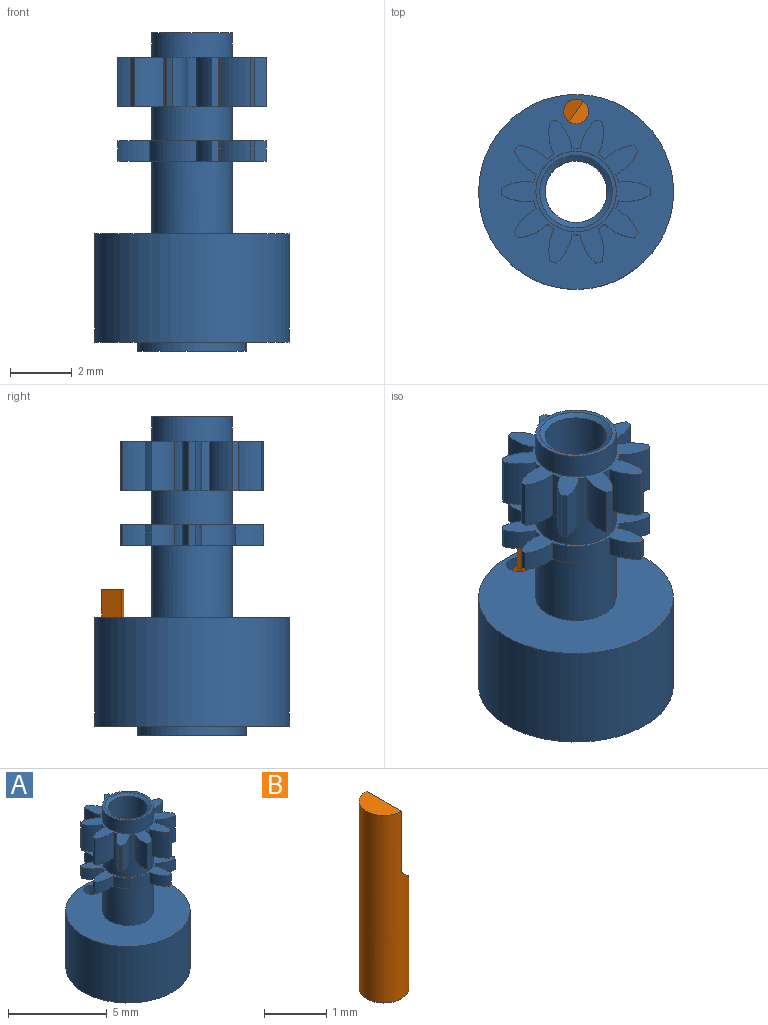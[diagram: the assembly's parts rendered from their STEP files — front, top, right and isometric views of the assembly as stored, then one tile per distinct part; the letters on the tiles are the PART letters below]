
ASSEMBLY  parts=2 mates=1
PART A: 89 faces, bbox 6.3x6.3x10.3 mm
  f0: cylinder r=1.3mm len=2.6mm, axis (0,0,-1), area 6.5mm2, adj f10,f47
  f1: cylinder r=1.3mm len=2.6mm, axis (0,0,-1), area 9mm2, adj f13,f88
  f2: cylinder r=1mm len=9.51mm, axis (0,0,-1), area 59.7mm2, adj f3,f12
  f3: cone r=1mm half-angle=30deg, axis (0,0,-1), area 6mm2, adj f2,f4
  f4: plane 3.5x3.5mm, normal (0,0,-1), area 3.5mm2, adj f3,f5
  f5: cylinder r=1.75mm len=3.5mm, axis (0,0,-1), area 3.3mm2, adj f4,f6
  f6: plane 6.3x6.3mm, normal (0,0,-1), area 21mm2, adj f5,f7,f11
  f7: cylinder r=3.15mm len=6.3mm, axis (0,0,-1), area 69.3mm2, adj f6,f8
  f8: plane 6.3x6.3mm, normal (0,0,1), area 25.4mm2, adj f7,f9,f11
  f9: cylinder r=1.3mm len=2.6mm, axis (0,0,-1), area 19.2mm2, adj f8,f46
  f10: plane 2.6x2.6mm, normal (0,0,1), area 1mm2, adj f0,f12
  f11: cylinder r=0.4mm len=3.5mm, axis (0,0,1), area 8.8mm2, adj f6,f8
  f12: cone r=1.17mm half-angle=60deg, axis (0,0,1), area 1.4mm2, adj f2,f10
  f13: plane 4.8x4.63mm, normal (0,0,1), area 5.2mm2, adj f1,f14,f15,f16,f17,f18,f19,f20
  f14: cylinder r=1.5mm len=1.03mm, axis (0,0,-1), area 0.7mm2, adj f13,f15,f45,f46
  f15: cylinder r=1.4mm len=1.5mm, axis (0,0,-1), area 1.3mm2, adj f13,f14,f16,f46
  f16: cylinder r=1.5mm len=0.92mm, axis (0,0,-1), area 0.7mm2, adj f13,f15,f17,f46
  f17: cylinder r=2.4mm len=0.65mm, axis (0,0,-1), area 0.1mm2, adj f13,f16,f18,f46
  f18: cylinder r=1.5mm len=1.04mm, axis (0,0,-1), area 0.7mm2, adj f13,f17,f19,f46
  f19: cylinder r=1.4mm len=0.65mm, axis (0,0,-1), area 0.2mm2, adj f13,f18,f20,f46
  f20: cylinder r=1.5mm len=0.95mm, axis (0,0,-1), area 0.7mm2, adj f13,f19,f21,f46
  f21: cylinder r=2.4mm len=0.65mm, axis (0,0,-1), area 0.1mm2, adj f13,f20,f22,f46
  f22: cylinder r=1.5mm len=0.77mm, axis (0,0,-1), area 0.7mm2, adj f13,f21,f23,f46
  f23: cylinder r=1.4mm len=0.65mm, axis (0,0,-1), area 0.2mm2, adj f13,f22,f24,f46
  f24: cylinder r=1.5mm len=1.03mm, axis (0,0,-1), area 0.7mm2, adj f13,f23,f25,f46
  f25: cylinder r=2.4mm len=0.65mm, axis (0,0,-1), area 0.1mm2, adj f13,f24,f26,f46
  f26: cylinder r=1.5mm len=1.03mm, axis (0,0,-1), area 0.7mm2, adj f13,f25,f27,f46
  f27: cylinder r=1.4mm len=0.65mm, axis (0,0,-1), area 0.2mm2, adj f13,f26,f28,f46
  f28: cylinder r=1.5mm len=0.77mm, axis (0,0,-1), area 0.7mm2, adj f13,f27,f29,f46
  f29: cylinder r=2.4mm len=0.65mm, axis (0,0,-1), area 0.1mm2, adj f13,f28,f30,f46
  f30: cylinder r=1.5mm len=0.95mm, axis (0,0,-1), area 0.7mm2, adj f13,f29,f31,f46
  f31: cylinder r=1.4mm len=0.65mm, axis (0,0,-1), area 0.2mm2, adj f13,f30,f32,f46
  f32: cylinder r=1.5mm len=1.04mm, axis (0,0,-1), area 0.7mm2, adj f13,f31,f33,f46
  f33: cylinder r=2.4mm len=0.65mm, axis (0,0,-1), area 0.1mm2, adj f13,f32,f34,f46
  f34: cylinder r=1.5mm len=0.92mm, axis (0,0,-1), area 0.7mm2, adj f13,f33,f35,f46
  f35: cylinder r=1.4mm len=0.65mm, axis (0,0,-1), area 0.2mm2, adj f13,f34,f36,f46
  f36: cylinder r=1.5mm len=0.92mm, axis (0,0,-1), area 0.7mm2, adj f13,f35,f37,f46
  f37: cylinder r=2.4mm len=0.65mm, axis (0,0,-1), area 0.1mm2, adj f13,f36,f38,f46
  f38: cylinder r=1.5mm len=1.04mm, axis (0,0,-1), area 0.7mm2, adj f13,f37,f39,f46
  f39: cylinder r=1.4mm len=0.65mm, axis (0,0,-1), area 0.2mm2, adj f13,f38,f40,f46
  f40: cylinder r=1.5mm len=0.95mm, axis (0,0,-1), area 0.7mm2, adj f13,f39,f41,f46
  f41: cylinder r=2.4mm len=0.65mm, axis (0,0,-1), area 0.1mm2, adj f13,f40,f42,f46
  f42: cylinder r=1.5mm len=0.77mm, axis (0,0,-1), area 0.7mm2, adj f13,f41,f43,f46
  f43: cylinder r=1.4mm len=0.65mm, axis (0,0,-1), area 0.2mm2, adj f13,f42,f44,f46
  f44: cylinder r=1.5mm len=1.03mm, axis (0,0,-1), area 0.7mm2, adj f13,f43,f45,f46
  f45: cylinder r=2.4mm len=0.65mm, axis (0,0,-1), area 0.1mm2, adj f13,f14,f44,f46
  f46: plane 4.8x4.63mm, normal (0,0,-1), area 5.2mm2, adj f9,f14,f15,f16,f17,f18,f19,f20
  f47: plane 4.8x4.63mm, normal (0,0,1), area 6.3mm2, adj f0,f48,f49,f50,f51,f52,f53,f54
  f48: cylinder r=1.5mm len=1.6mm, axis (0,0,-1), area 1.7mm2, adj f47,f49,f87,f88
  f49: cylinder r=1.4mm len=1.6mm, axis (0,0,-1), area 0.4mm2, adj f47,f48,f50,f88
  f50: cylinder r=1.5mm len=1.6mm, axis (0,0,-1), area 1.7mm2, adj f47,f49,f54,f88
  f51: cylinder r=1.5mm len=1.6mm, axis (0,0,-1), area 1.7mm2, adj f47,f52,f54,f88
  f52: cylinder r=1.4mm len=1.6mm, axis (0,0,-1), area 0.4mm2, adj f47,f51,f53,f88
  f53: cylinder r=1.5mm len=1.6mm, axis (0,0,-1), area 1.7mm2, adj f47,f52,f58,f88
  f54: cylinder r=2.4mm len=1.6mm, axis (0,0,-1), area 0.3mm2, adj f47,f50,f51,f88
  f55: cylinder r=1.5mm len=1.6mm, axis (0,0,-1), area 1.7mm2, adj f47,f56,f58,f88
  f56: cylinder r=1.4mm len=1.6mm, axis (0,0,-1), area 0.4mm2, adj f47,f55,f57,f88
  f57: cylinder r=1.5mm len=1.6mm, axis (0,0,-1), area 1.7mm2, adj f47,f56,f62,f88
  f58: cylinder r=2.4mm len=1.6mm, axis (0,0,-1), area 0.3mm2, adj f47,f53,f55,f88
  f59: cylinder r=1.5mm len=1.6mm, axis (0,0,-1), area 1.7mm2, adj f47,f60,f62,f88
  f60: cylinder r=1.4mm len=1.6mm, axis (0,0,-1), area 0.4mm2, adj f47,f59,f61,f88
  f61: cylinder r=1.5mm len=1.6mm, axis (0,0,-1), area 1.7mm2, adj f47,f60,f66,f88
  f62: cylinder r=2.4mm len=1.6mm, axis (0,0,-1), area 0.3mm2, adj f47,f57,f59,f88
  f63: cylinder r=1.5mm len=1.6mm, axis (0,0,-1), area 1.7mm2, adj f47,f64,f66,f88
  f64: cylinder r=1.4mm len=1.6mm, axis (0,0,-1), area 0.4mm2, adj f47,f63,f65,f88
  f65: cylinder r=1.5mm len=1.6mm, axis (0,0,-1), area 1.7mm2, adj f47,f64,f70,f88
  f66: cylinder r=2.4mm len=1.6mm, axis (0,0,-1), area 0.3mm2, adj f47,f61,f63,f88
  f67: cylinder r=1.5mm len=1.6mm, axis (0,0,-1), area 1.7mm2, adj f47,f68,f70,f88
  f68: cylinder r=1.4mm len=1.6mm, axis (0,0,-1), area 0.4mm2, adj f47,f67,f69,f88
  f69: cylinder r=1.5mm len=1.6mm, axis (0,0,-1), area 1.7mm2, adj f47,f68,f74,f88
  f70: cylinder r=2.4mm len=1.6mm, axis (0,0,-1), area 0.3mm2, adj f47,f65,f67,f88
  f71: cylinder r=1.5mm len=1.6mm, axis (0,0,-1), area 1.7mm2, adj f47,f72,f74,f88
  f72: cylinder r=1.4mm len=1.6mm, axis (0,0,-1), area 0.4mm2, adj f47,f71,f73,f88
  f73: cylinder r=1.5mm len=1.6mm, axis (0,0,-1), area 1.7mm2, adj f47,f72,f78,f88
  f74: cylinder r=2.4mm len=1.6mm, axis (0,0,-1), area 0.3mm2, adj f47,f69,f71,f88
  f75: cylinder r=1.5mm len=1.6mm, axis (0,0,-1), area 1.7mm2, adj f47,f76,f78,f88
  f76: cylinder r=1.4mm len=1.6mm, axis (0,0,-1), area 0.4mm2, adj f47,f75,f77,f88
  f77: cylinder r=1.5mm len=1.6mm, axis (0,0,-1), area 1.7mm2, adj f47,f76,f82,f88
  f78: cylinder r=2.4mm len=1.6mm, axis (0,0,-1), area 0.3mm2, adj f47,f73,f75,f88
  f79: cylinder r=1.5mm len=1.6mm, axis (0,0,-1), area 1.7mm2, adj f47,f80,f82,f88
  f80: cylinder r=1.4mm len=1.6mm, axis (0,0,-1), area 0.4mm2, adj f47,f79,f81,f88
  f81: cylinder r=1.5mm len=1.6mm, axis (0,0,-1), area 1.7mm2, adj f47,f80,f86,f88
  f82: cylinder r=2.4mm len=1.6mm, axis (0,0,-1), area 0.3mm2, adj f47,f77,f79,f88
  f83: cylinder r=1.5mm len=1.6mm, axis (0,0,-1), area 1.7mm2, adj f47,f84,f86,f88
  f84: cylinder r=1.4mm len=1.6mm, axis (0,0,-1), area 0.4mm2, adj f47,f83,f85,f88
  f85: cylinder r=1.5mm len=1.6mm, axis (0,0,-1), area 1.7mm2, adj f47,f84,f87,f88
  f86: cylinder r=2.4mm len=1.6mm, axis (0,0,-1), area 0.3mm2, adj f47,f81,f83,f88
  f87: cylinder r=2.4mm len=1.6mm, axis (0,0,-1), area 0.3mm2, adj f47,f48,f85,f88
  f88: plane 4.8x4.63mm, normal (0,0,-1), area 6.3mm2, adj f1,f48,f49,f50,f51,f52,f53,f54
PART B: 5 faces, bbox 0.8x0.8x3.7 mm
  f0: cylinder r=0.4mm len=3.7mm, axis (0,0,-1), area 7.5mm2, adj f1,f2,f3,f4
  f1: plane 0.8x0.4mm, normal (0,0,1), area 0.3mm2, adj f0,f3
  f2: plane 0.8x0.8mm, normal (0,0,-1), area 0.5mm2, adj f0
  f3: plane 1.2x0.8mm, normal (1,0,0), area 1mm2, adj f0,f1,f4
  f4: plane 0.8x0.4mm, normal (0.71,0,0.71), area 0.4mm2, adj f0,f3
PLACE A at identity fixed
PLACE B rot(axis=(0,0,1),144deg) t=(0,2.6,1)mm
MATE fastened B.f0 <-> A.f11  axis (0,0,-1) through (0,2.6,4.7)mm
